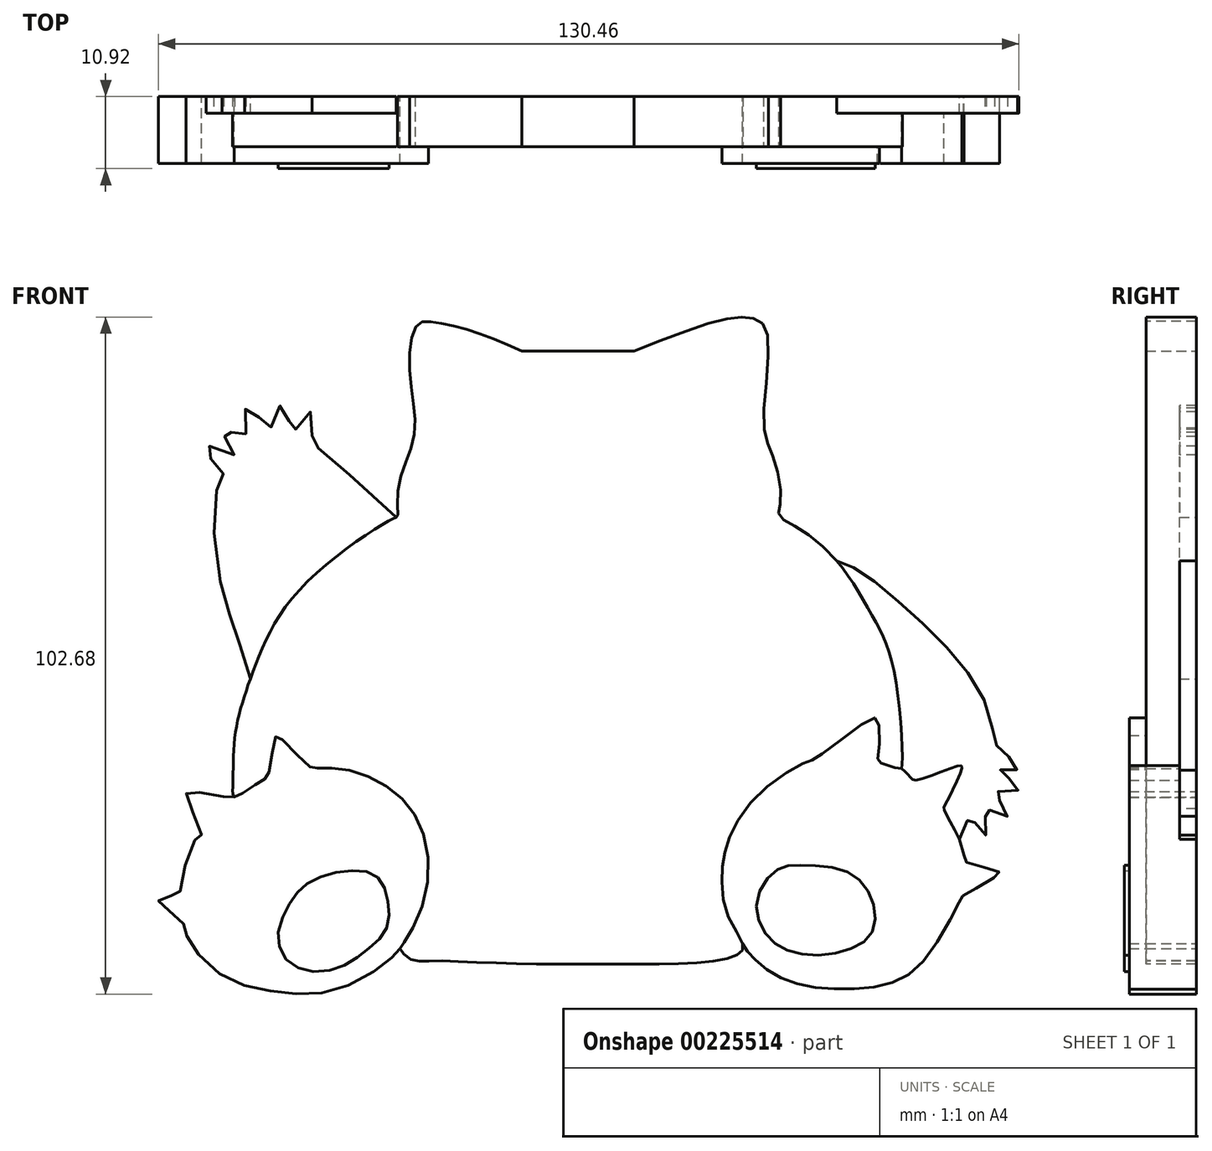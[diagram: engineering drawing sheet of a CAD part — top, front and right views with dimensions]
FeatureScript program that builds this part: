
annotation { "Feature Type Name" : "Feature", "Feature Type Description" : "" }
export const myFeature = defineFeature(function(context is Context, id is Id, definition is map)
    precondition{}
    {
        {
            var Q0;
            Q0=qCreatedBy(makeId("Front.planeOp"),FACE);
            var sketch = newSketch(context, id + "F0", { "sketchPlane" : qUnion([Q0])});
            skLineSegment(sketch, "E0", {"start": v(-8.61, 47.77) * mm, "end": v(8.41, 47.77) * mm});
            skFitSpline(sketch, "E1", {"points": [v(8.41, 47.77) * mm, v(22.45, 52.65) * mm, v(26.64, 52.65) * mm, v(28.6, 50.48) * mm, v(28.08, 36.69) * mm, v(29.45, 31.86) * mm, v(30.62, 25.07) * mm, v(30.36, 22.9) * mm, v(32.9, 21.14) * mm, v(39.13, 15.95) * mm, v(44.73, 7.25) * mm, v(47.95, -1.35) * mm, v(48.99, -15.53) * mm, v(48.6, -15.62) * mm, v(45.4, -14.49) * mm, v(45.4, -14.02) * mm, v(45.4, -8.35) * mm, v(44.45, -7.97) * mm, v(36.13, -13.92) * mm, v(34.71, -14.49) * mm, v(27.34, -19.4) * mm, v(22.61, -26.68) * mm, v(21.76, -31.31) * mm, v(22.52, -37.55) * mm, v(24.87, -42.1) * mm, v(24.5, -43.5) * mm, v(19.02, -44.92) * mm, v(4.56, -45.2) * mm, v(-10.75, -45.11) * mm, v(-22.28, -44.73) * mm, v(-25.5, -44.45) * mm, v(-27.1, -42.84) * mm, v(-26.63, -42.09) * mm, v(-23.32, -35.1) * mm, v(-23.89, -24.5) * mm, v(-28.8, -18.46) * mm, v(-35.7, -15.62) * mm, v(-39.86, -15.53) * mm, v(-41, -15.15) * mm, v(-45.63, -10.61) * mm, v(-46, -10.9) * mm, v(-47.14, -16.66) * mm, v(-47.61, -17.14) * mm, v(-50.35, -18.93) * mm, v(-52.24, -19.88) * mm, v(-52.43, -18.08) * mm, v(-52.05, -10.24) * mm, v(-49.4, -0.97) * mm, v(-41.56, 12.35) * mm, v(-27.67, 22.56) * mm, v(-27.46, 22.64) * mm, v(-27.3, 27.38) * mm, v(-24.93, 34.94) * mm, v(-25.59, 44.49) * mm, v(-24.45, 51.77) * mm, v(-22, 52.15) * mm, v(-16.23, 50.82) * mm, v(-8.61, 47.77) * mm], "startDerivative": vector(557, 220.12) * mm, "endDerivative": vector(362.34, -160.51) * mm});
            skFitSpline(sketch, "E2", {"points": [v(24.87, -42.1) * mm, v(25.78, -43.53) * mm, v(28.43, -45.97) * mm, v(33.43, -48.27) * mm, v(40.37, -49.01) * mm, v(47.66, -48) * mm, v(53.35, -43.41) * mm, v(57.87, -35.4) * mm, v(58.38, -34.8) * mm, v(63.59, -31.71) * mm, v(63.74, -31.24) * mm, v(58.59, -29.63) * mm, v(58.4, -28.3) * mm, v(55.5, -21.92) * mm, v(55.57, -21.12) * mm, v(58.12, -15.54) * mm, v(57.88, -15.11) * mm, v(51.13, -17.33) * mm, v(50.27, -16.82) * mm, v(48.99, -15.53) * mm], "startDerivative": vector(21.94, -49.7) * mm, "endDerivative": vector(-39.9, 36) * mm});
            skFitSpline(sketch, "E3", {"points": [v(-52.24, -19.88) * mm, v(-53.35, -19.88) * mm, v(-59.15, -19.07) * mm, v(-59.42, -19.88) * mm, v(-57.19, -25.94) * mm, v(-58.17, -26.39) * mm, v(-60.49, -34.42) * mm, v(-60.58, -34.5) * mm, v(-63.52, -35.4) * mm, v(-63.61, -35.84) * mm, v(-60.04, -38.88) * mm, v(-59.42, -40.93) * mm, v(-54.07, -46.9) * mm, v(-45.23, -49.5) * mm, v(-36.58, -49.05) * mm, v(-28.64, -44.5) * mm, v(-27.1, -42.84) * mm], "startDerivative": vector(-21.49, -3.42) * mm, "endDerivative": vector(22.86, 29.6) * mm});
            skFitSpline(sketch, "E4", {"points": [v(-49.78, -1.98) * mm, v(-52.24, 5.86) * mm, v(-54.28, 12.64) * mm, v(-54.9, 26.65) * mm, v(-53.83, 28.97) * mm, v(-54.9, 30.13) * mm, v(-56.42, 32.8) * mm, v(-56.24, 33.34) * mm, v(-52.24, 32) * mm, v(-52.24, 32.27) * mm, v(-54.1, 35.75) * mm, v(-53.83, 35.84) * mm, v(-50.53, 34.77) * mm, v(-50.44, 35.04) * mm, v(-50.53, 38.96) * mm, v(-50, 38.96) * mm, v(-47.5, 36.73) * mm, v(-46.7, 36.1) * mm, v(-45.36, 39.4) * mm, v(-44.73, 39.14) * mm, v(-43.57, 35.84) * mm, v(-43.3, 35.48) * mm, v(-40.9, 38.52) * mm, v(-40.45, 37.98) * mm, v(-40.36, 33.6) * mm, v(-39.92, 33.25) * mm, v(-27.67, 22.56) * mm], "startDerivative": vector(-37.47, 124) * mm, "endDerivative": vector(171.98, -158) * mm});
            skFitSpline(sketch, "E5", {"points": [v(39.13, 15.95) * mm, v(42.32, 14.58) * mm, v(48.74, 9.57) * mm, v(56.56, 2.01) * mm, v(61.97, -6.34) * mm, v(63.3, -11.89) * mm, v(63.84, -12.42) * mm, v(66.58, -15.5) * mm, v(66.25, -15.76) * mm, v(63.78, -15.76) * mm, v(63.84, -15.83) * mm, v(66.65, -18.5) * mm, v(66.59, -18.88) * mm, v(63.14, -19.05) * mm, v(63.1, -19.12) * mm, v(65.05, -22.57) * mm, v(64.84, -22.82) * mm, v(61.73, -21.66) * mm, v(61.6, -21.92) * mm, v(61.79, -25.58) * mm, v(61.54, -25.61) * mm, v(59.44, -22.99) * mm, v(59.14, -23.1) * mm, v(57.72, -26.27) * mm], "startDerivative": vector(56.93, -19.06) * mm, "endDerivative": vector(-31.96, -76.67) * mm});
            skSolve(sketch);
        }
        {
            var Q0;
            Q0=makeQuery(id+"F0.imprint","IMPRINT",FACE,{"disambiguationData":[TD([[makeQuery(id+"F0.imprint","IMPRINT",EDGE,{"derivedFrom":sQuery(id+"F0.wireOp",EDGE,"E0")}),-1.0]])]});
            extrude(context, id + "F1", {"entities" : qUnion([Q0]), "depth" : 7.62 * mm});
        }
        {
            var Q0;
            {var subQ0=sQuery(id+"F0.wireOp",EDGE,"E4");Q0=makeQuery(id+"F0.imprint","IMPRINT",FACE,{"disambiguationData":[TD([[makeQuery(id+"F0.imprint","IMPRINT",EDGE,{"derivedFrom":subQ0}),-1.0]])]});}
            var Q1;
            {var subQ3=sQuery(id+"F0.wireOp",EDGE,"E5");Q1=makeQuery(id+"F0.imprint","IMPRINT",FACE,{"disambiguationData":[TD([[makeQuery(id+"F0.imprint","IMPRINT",EDGE,{"derivedFrom":subQ3}),-1.0]])]});}
            extrude(context, id + "F2", {"entities" : qUnion([Q0, Q1]), "operationType" : NewBodyOperationType.ADD, "depth" : 2.54 * mm});
        }
        {
            var Q0;
            {var subQ0=sQuery(id+"F0.wireOp",EDGE,"E3");Q0=makeQuery(id+"F0.imprint","IMPRINT",FACE,{"disambiguationData":[TD([[makeQuery(id+"F0.imprint","IMPRINT",EDGE,{"derivedFrom":subQ0}),1.0]])]});}
            extrude(context, id + "F3", {"entities" : qUnion([Q0]), "operationType" : NewBodyOperationType.ADD, "depth" : 10.16 * mm});
        }
        {
            var Q0;
            {var subQ0=sQuery(id+"F0.wireOp",EDGE,"E2");var subQ1=sQuery(id+"F0.wireOp",EDGE,"E1");var subQ2=makeQuery(id+"F0.imprint","INTERSECT",VERTEX,{"disambiguationData":[OD(0.0)],"derivedFrom":[subQ1,subQ0]});Q0=makeQuery(id+"F0.imprint","IMPRINT",FACE,{"disambiguationData":[TD([[makeQuery(id+"F0.imprint","IMPRINT",EDGE,{"disambiguationData":[TD([[subQ2,1.0]])],"derivedFrom":subQ1}),1.0]])]});}
            extrude(context, id + "F4", {"entities" : qUnion([Q0]), "operationType" : NewBodyOperationType.ADD, "depth" : 10.16 * mm});
        }
        {
            var Q0;
            Q0=makeQuery(id+"F3.opExtrude","CAP_FACE",FACE,{"disambiguationData":[OSD([sQuery(id+"F0.wireOp",EDGE,"E1"),sQuery(id+"F0.wireOp",EDGE,"E3")])],"isStart":false});
            var sketch = newSketch(context, id + "F5", { "sketchPlane" : qUnion([Q0])});
            skFitSpline(sketch, "E6", {"points": [v(-43.83, -36.05) * mm, v(-40.88, -32.85) * mm, v(-35.07, -31.08) * mm, v(-30.6, -31.93) * mm, v(-28.92, -35.63) * mm, v(-29.26, -40) * mm, v(-32.37, -43.3) * mm, v(-37.26, -46.07) * mm, v(-43.15, -45.48) * mm, v(-45.6, -41.36) * mm, v(-43.83, -36.05) * mm]});
            skFitSpline(sketch, "E7", {"points": [v(30.2, -30.83) * mm, v(33.73, -30.24) * mm, v(40.63, -31.17) * mm, v(44.34, -35.04) * mm, v(44.6, -40.18) * mm, v(40.38, -43.2) * mm, v(32.97, -43.55) * mm, v(28.5, -40.77) * mm, v(27.08, -35.46) * mm, v(30.2, -30.83) * mm]});
            skSolve(sketch);
        }
        {
            var Q0;
            Q0=makeQuery(id+"F5.imprint","IMPRINT",FACE,{"disambiguationData":[TD([[makeQuery(id+"F5.imprint","IMPRINT",EDGE,{"derivedFrom":sQuery(id+"F5.wireOp",EDGE,"E6")}),-1.0]])]});
            var Q1;
            Q1=makeQuery(id+"F5.imprint","IMPRINT",FACE,{"disambiguationData":[TD([[makeQuery(id+"F5.imprint","IMPRINT",EDGE,{"derivedFrom":sQuery(id+"F5.wireOp",EDGE,"E7")}),-1.0]])]});
            extrude(context, id + "F6", {"entities" : qUnion([Q0, Q1]), "operationType" : NewBodyOperationType.ADD, "depth" : 0.76 * mm});
        }
    });
